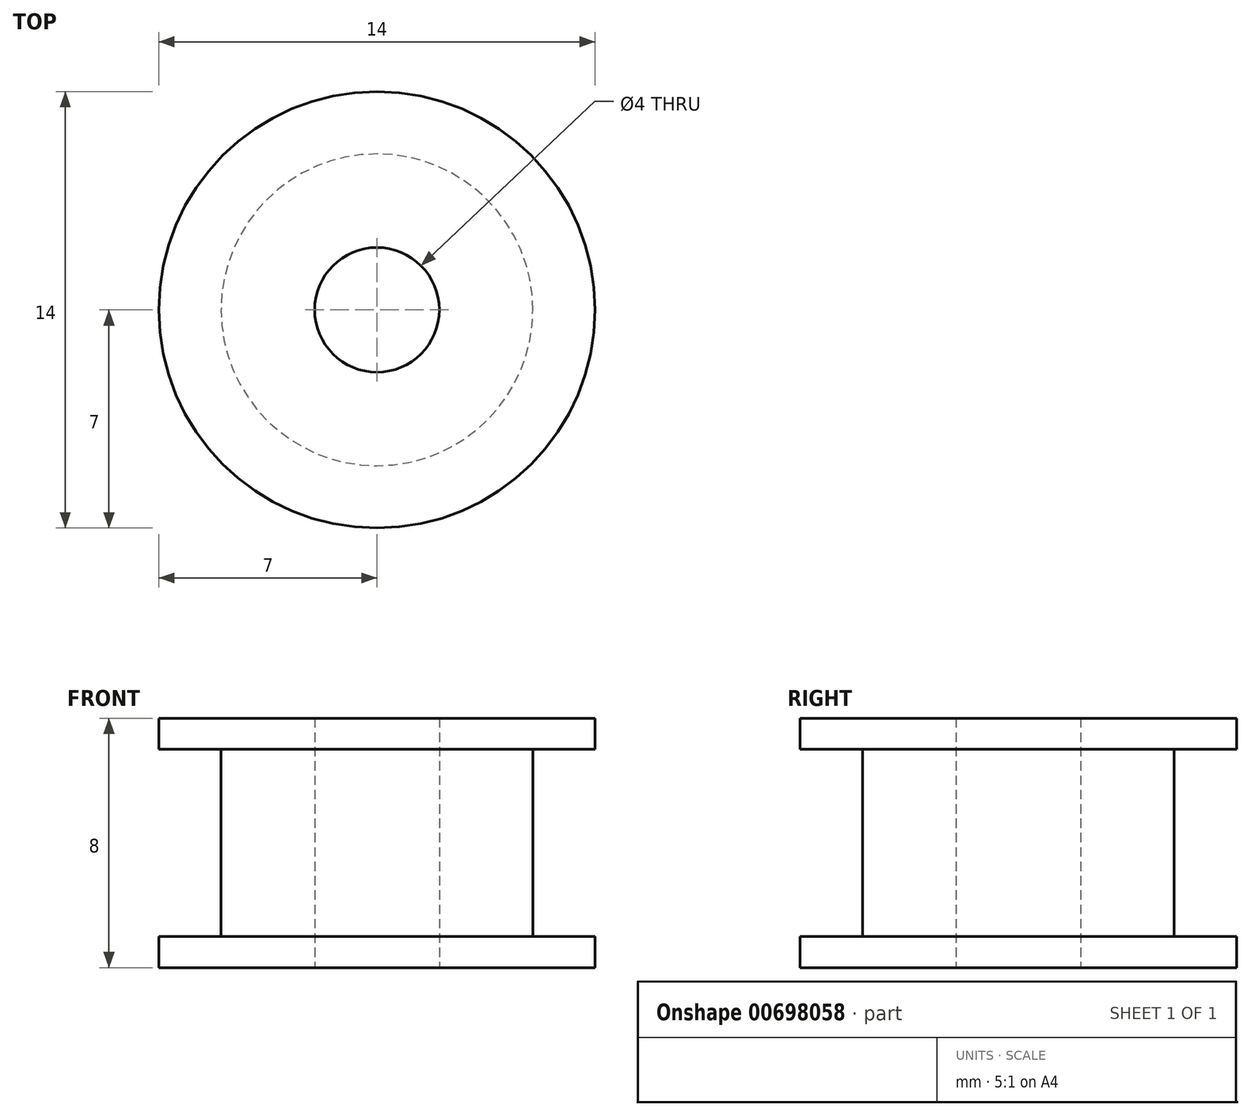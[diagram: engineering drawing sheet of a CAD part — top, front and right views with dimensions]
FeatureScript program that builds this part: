
annotation { "Feature Type Name" : "Feature", "Feature Type Description" : "" }
export const myFeature = defineFeature(function(context is Context, id is Id, definition is map)
    precondition{}
    {
        {
            var Q0;
            Q0=qCreatedBy(makeId("Top.planeOp"),FACE);
            var sketch = newSketch(context, id + "F0", { "sketchPlane" : qUnion([Q0])});
            skCircle(sketch, "E0", {"center": v(0, 0) * mm, "radius": 5 * mm});
            skCircle(sketch, "E1", {"center": v(0, 0) * mm, "radius": 7 * mm});
            skCircle(sketch, "E2", {"center": v(0, 0) * mm, "radius": 2 * mm});
            skSolve(sketch);
        }
        {
            var Q0;
            Q0=makeQuery(id+"F0.imprint","IMPRINT",FACE,{"disambiguationData":[TD([[makeQuery(id+"F0.imprint","IMPRINT",EDGE,{"derivedFrom":sQuery(id+"F0.wireOp",EDGE,"E0")}),1.0]])]});
            extrude(context, id + "F1", {"entities" : qUnion([Q0]), "depth" : 8 * mm, "offsetDistance" : 25 * mm});
        }
        {
            var Q0;
            Q0=makeQuery(id+"F0.imprint","IMPRINT",FACE,{"disambiguationData":[TD([[makeQuery(id+"F0.imprint","IMPRINT",EDGE,{"derivedFrom":sQuery(id+"F0.wireOp",EDGE,"E0")}),-1.0]])]});
            extrude(context, id + "F2", {"entities" : qUnion([Q0]), "operationType" : NewBodyOperationType.ADD, "depth" : 1 * mm, "offsetDistance" : 25 * mm});
        }
        {
            var Q0;
            Q0=makeQuery(id+"F1.opExtrude","CAP_FACE",FACE,{"disambiguationData":[OSD([sQuery(id+"F0.wireOp",EDGE,"E0")])],"isStart":false});
            var sketch = newSketch(context, id + "F3", { "sketchPlane" : qUnion([Q0])});
            skCircle(sketch, "E3", {"center": v(0, 0) * mm, "radius": 7 * mm});
            skSolve(sketch);
        }
        {
            var Q0;
            Q0=makeQuery(id+"F3.imprint","IMPRINT",FACE,{"disambiguationData":[TD([[makeQuery(id+"F3.imprint","IMPRINT",EDGE,{"derivedFrom":sQuery(id+"F3.wireOp",EDGE,"E3")}),1.0]])]});
            extrude(context, id + "F4", {"entities" : qUnion([Q0]), "operationType" : NewBodyOperationType.ADD, "oppositeDirection" : true, "depth" : 1 * mm, "offsetDistance" : 25 * mm});
        }
    });
